# Revit family: NBS_TapcoRoofingProducts_DryFxngVrgs_TapcoSlate_DryVergeJointingClip
name_source: partatom
category: Generic Models
units: mm (PartAtom-declared; Revit-internal decimal feet)

## family parameters
Always vertical = Yes
Can host rebar = No
Cut with Voids When Loaded = No
Part Type = Normal
Room Calculation Point = No
Round Connector Dimension = Use Diameter
Shared = No
Work Plane-Based = No

## types (1)
- TapcoSlate_DryVergeJointingClip
    Applications = Used to clip together the joints in the TapcoSlate - Dry Verge system
    AssetType = Fixed
    BIMObjectName = NBS_TapcoRoofingProducts_DryFixingVerges_TapcoSlate_DryVergeJointingClip
    Category = Pr_35_90_93_30:Dry fixing verges
    Color = Black
    Combustible = Yes
    Description = A one-size-fits-all jointing clip that can be scored and then bent accordingly
    DurationUnit = year
    ExpectedLife = 25+ years
    Features = Wind uplift and rain protection, patented ‘Drip System’ allows for self drainage of rain water into the gutter, requires no maintenance once installed, easy and quick to install
    IfcExportAs = IfcCoveringType
    IfcExportType = ROOFING
    IsExternal = Yes
    JointingClipMaterial = NBS_TapcoRoofingProducts_PVC-U_Black
    ManufacturerName = Tapco Roofing Products
    ManufacturerURL = www.tapcoroofingproducts.com
    Material = Unplasticised polyvinyl chloride (PVC-U)
    ModelReference = TapcoSlate_DryVergeJointingClip
    NBSCertification = www.nationalbimlibrary.com/cert/ck5qqsia
    NBSDescription = Dry fixing verges
    NBSReference = 45-80-90/378
    Name = DryFixingVerges_TapcoSlate_DryVergeJointingClip_TapcoRoofingProducts
    NominalHeight = 70 mm
    NominalLength = 90 mm
    NominalWidth = 40 mm
    ProductInformation = https://www.tapcoroofingproducts.com
    ReplacementCost = 2.21
    Size = Multifaceted
    Status = UNSET
    ThermalTransmittance = 0
    Uniclass2015Code = Pr_35_90_93_30
    Uniclass2015Title = Dry fixing verges
    Uniclass2015Version = Products v1.20
    Version = 1
    WarrantyDescription = 40-years
    WarrantyDurationUnit = year

## geometry (parser evidence)
native form markers: Sweep x2
no freeform markers — native parametric forms only
